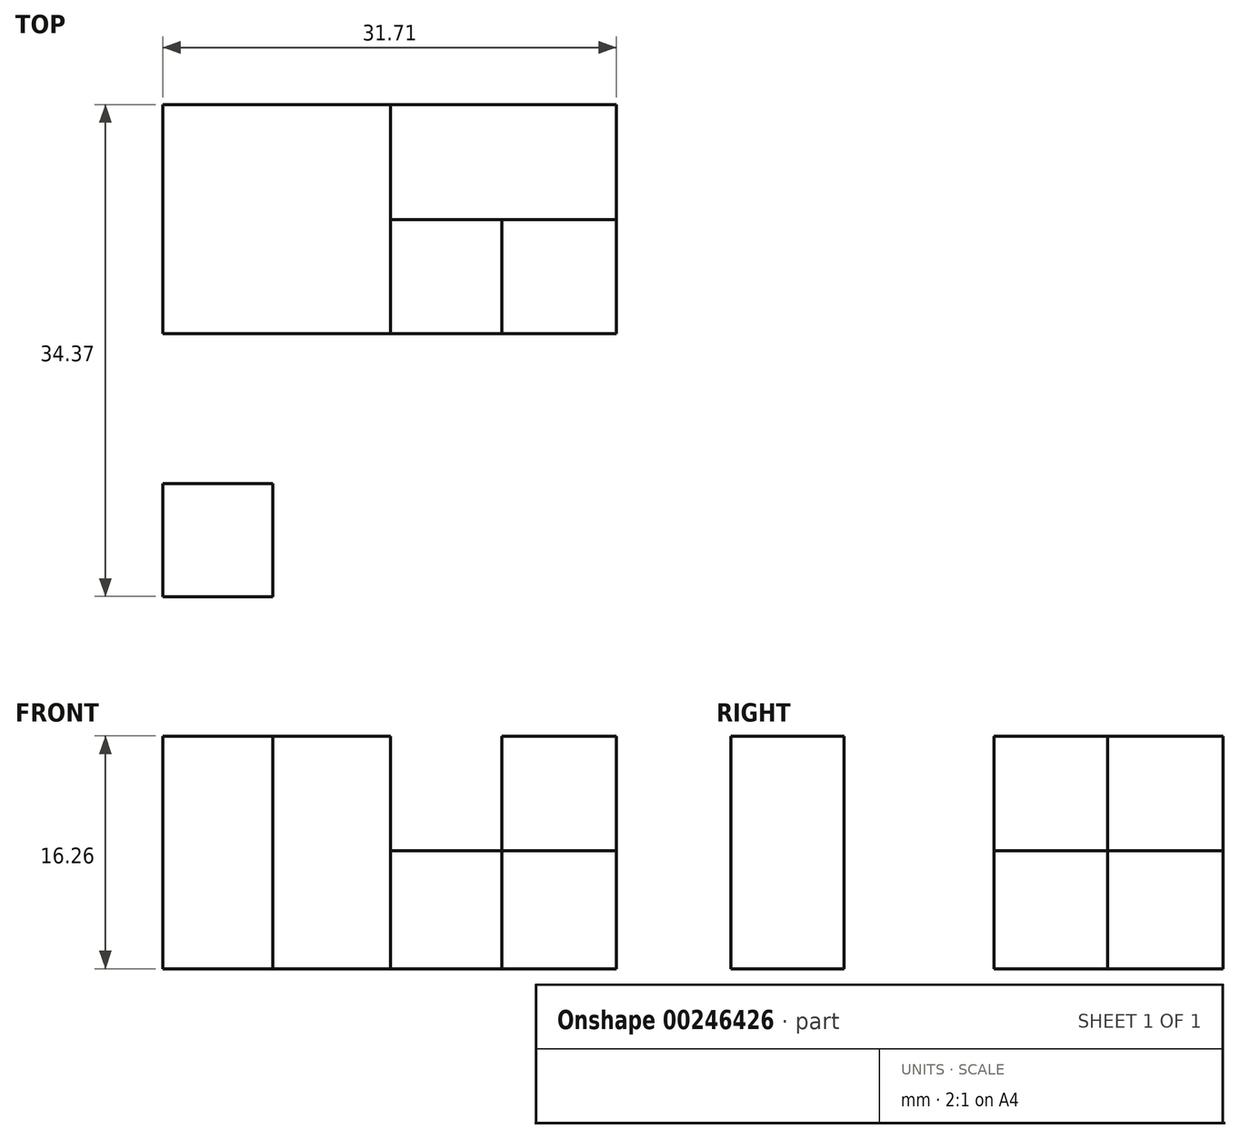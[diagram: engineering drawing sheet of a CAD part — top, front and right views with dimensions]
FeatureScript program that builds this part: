
annotation { "Feature Type Name" : "Feature", "Feature Type Description" : "" }
export const myFeature = defineFeature(function(context is Context, id is Id, definition is map)
    precondition{}
    {
        {
            var Q0;
            Q0=qCreatedBy(makeId("Top.planeOp"),FACE);
            var sketch = newSketch(context, id + "F0", { "sketchPlane" : qUnion([Q0])});
            skLineSegment(sketch, "E0", {"start": v(-16.97, -8.44) * mm, "end": v(-9.26, -8.44) * mm});
            skLineSegment(sketch, "E1", {"start": v(-1.06, 9.92) * mm, "end": v(14.74, 9.92) * mm});
            skLineSegment(sketch, "E2", {"start": v(14.74, 9.92) * mm, "end": v(14.74, 25.93) * mm});
            skLineSegment(sketch, "E3", {"start": v(14.74, 25.93) * mm, "end": v(-16.97, 25.93) * mm});
            skLineSegment(sketch, "E4", {"start": v(-16.97, 25.93) * mm, "end": v(-16.97, -8.44) * mm});
            skPoint(sketch, "E5", {"position": v(-9.26, -0.55) * mm});
            skLineSegment(sketch, "E6", {"start": v(-9.26, -0.55) * mm, "end": v(-16.97, -0.55) * mm});
            skLineSegment(sketch, "E7", {"start": v(-1.06, 9.92) * mm, "end": v(-16.97, 9.92) * mm});
            skLineSegment(sketch, "E8", {"start": v(-1.06, 9.92) * mm, "end": v(-1.06, 25.93) * mm});
            skPoint(sketch, "E9", {"position": v(6.72, 9.92) * mm});
            skPoint(sketch, "E10", {"position": v(14.74, 17.88) * mm});
            skLineSegment(sketch, "E11", {"start": v(14.74, 17.88) * mm, "end": v(-1.06, 17.88) * mm});
            skLineSegment(sketch, "E12", {"start": v(6.72, 9.92) * mm, "end": v(6.72, 17.88) * mm});
            skLineSegment(sketch, "E13", {"start": v(-9.26, -8.44) * mm, "end": v(-9.26, 9.92) * mm});
            skSolve(sketch);
        }
        {
            var Q0;
            {var subQ0=sQuery(id+"F0.wireOp",EDGE,"E0");Q0=makeQuery(id+"F0.imprint","IMPRINT",FACE,{"disambiguationData":[TD([[makeQuery(id+"F0.imprint","IMPRINT",EDGE,{"derivedFrom":subQ0}),1.0]])]});}
            extrude(context, id + "F1", {"entities" : qUnion([Q0]), "depth" : 16.26 * mm});
        }
        {
            var Q0;
            {var subQ1=sQuery(id+"F0.wireOp",EDGE,"E4");var subQ6=sQuery(id+"F0.wireOp",EDGE,"E3");var subQ7=makeQuery(id+"F0.imprint","INTERSECT",VERTEX,{"derivedFrom":[subQ6,subQ1]});Q0=makeQuery(id+"F0.imprint","IMPRINT",FACE,{"disambiguationData":[TD([[makeQuery(id+"F0.imprint","IMPRINT",EDGE,{"disambiguationData":[TD([[subQ7,1.0]])],"derivedFrom":subQ6}),1.0]])]});}
            extrude(context, id + "F2", {"entities" : qUnion([Q0]), "depth" : 16.26 * mm});
        }
        {
            var Q0;
            {var subQ3=sQuery(id+"F0.wireOp",EDGE,"E12");Q0=makeQuery(id+"F0.imprint","IMPRINT",FACE,{"disambiguationData":[TD([[makeQuery(id+"F0.imprint","IMPRINT",EDGE,{"derivedFrom":subQ3}),-1.0]])]});}
            extrude(context, id + "F3", {"entities" : qUnion([Q0]), "depth" : 16.26 * mm});
        }
        {
            var Q0;
            {var subQ1=sQuery(id+"F0.wireOp",EDGE,"E2");var subQ5=sQuery(id+"F0.wireOp",EDGE,"E3");var subQ8=makeQuery(id+"F0.imprint","INTERSECT",VERTEX,{"derivedFrom":[subQ1,subQ5]});Q0=makeQuery(id+"F0.imprint","IMPRINT",FACE,{"disambiguationData":[TD([[makeQuery(id+"F0.imprint","IMPRINT",EDGE,{"disambiguationData":[TD([[subQ8,1.0]])],"derivedFrom":subQ1}),1.0]])]});}
            extrude(context, id + "F4", {"entities" : qUnion([Q0]), "depth" : 8.24 * mm});
        }
        {
            var Q0;
            Q0=makeQuery(id+"F4.opExtrude","SWEPT_FACE",FACE,{"disambiguationData":[OSD([sQuery(id+"F0.wireOp",EDGE,"E11")])]});
            var Q1;
            Q1=makeQuery(id+"F2.opExtrude","SWEPT_FACE",FACE,{"disambiguationData":[OSD([sQuery(id+"F0.wireOp",EDGE,"E7")])]});
            extrude(context, id + "F5", {"entities" : qUnion([Q0]), "endBound" : BoundingType.UP_TO_SURFACE, "endBoundEntityFace" : qUnion([Q1]), "depth" : 7.11 * mm});
        }
    });
